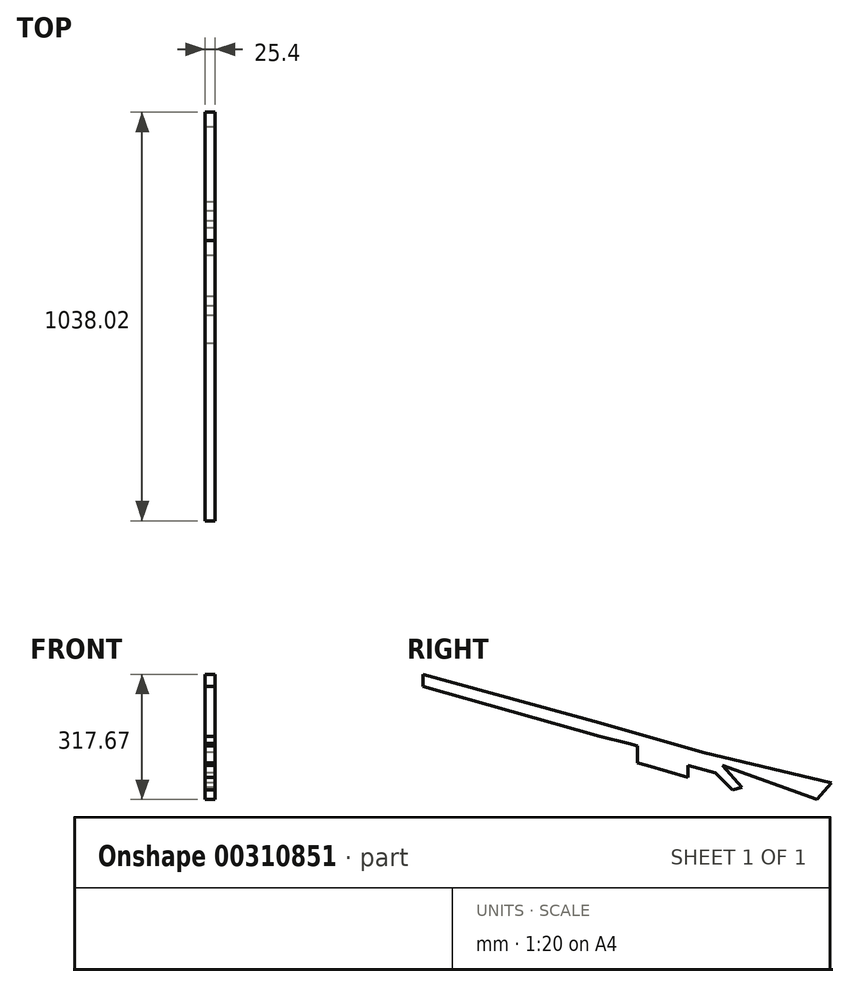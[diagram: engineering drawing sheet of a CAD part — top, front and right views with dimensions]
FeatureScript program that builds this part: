
annotation { "Feature Type Name" : "Feature", "Feature Type Description" : "" }
export const myFeature = defineFeature(function(context is Context, id is Id, definition is map)
    precondition{}
    {
        {
            var Q0;
            Q0=qCreatedBy(makeId("Right.planeOp"),FACE);
            var sketch = newSketch(context, id + "F0", { "sketchPlane" : qUnion([Q0])});
            skLineSegment(sketch, "E0", {"start": v(0, 0) * mm, "end": v(191.87, -55.13) * mm});
            skLineSegment(sketch, "E1", {"start": v(191.87, -55.13) * mm, "end": v(240.84, -111.58) * mm});
            skLineSegment(sketch, "E2", {"start": v(240.84, -111.58) * mm, "end": v(217.53, -117.95) * mm});
            skLineSegment(sketch, "E3", {"start": v(217.53, -117.95) * mm, "end": v(174.26, -75.25) * mm});
            skLineSegment(sketch, "E4", {"start": v(174.26, -75.25) * mm, "end": v(104.37, -55.13) * mm});
            skLineSegment(sketch, "E5", {"start": v(104.37, -55.13) * mm, "end": v(104.37, -86.25) * mm});
            skLineSegment(sketch, "E6", {"start": v(104.37, -86.25) * mm, "end": v(0, -55.13) * mm});
            skLineSegment(sketch, "E7", {"start": v(0, -55.13) * mm, "end": v(0, 0) * mm});
            skLineSegment(sketch, "E8", {"start": v(0, 0) * mm, "end": v(-47.42, 14.1) * mm});
            skLineSegment(sketch, "E9", {"start": v(-47.42, 14.1) * mm, "end": v(-47.42, 0) * mm});
            skLineSegment(sketch, "E10", {"start": v(-47.42, 0) * mm, "end": v(0, -12.5) * mm});
            skLineSegment(sketch, "E11", {"start": v(0, -12.5) * mm, "end": v(0, -55.13) * mm});
            skLineSegment(sketch, "E12", {"start": v(0, -55.13) * mm, "end": v(-23.7, -49.55) * mm});
            skPoint(sketch, "E12.endSnap0", {"position": v(-23.7, -6.25) * mm});
            skLineSegment(sketch, "E13", {"start": v(-23.7, -49.55) * mm, "end": v(-23.7, -6.25) * mm});
            skLineSegment(sketch, "E14", {"start": v(191.87, -55.13) * mm, "end": v(142.53, -22.53) * mm});
            skLineSegment(sketch, "E15", {"start": v(142.53, -22.53) * mm, "end": v(-51.75, 32.66) * mm});
            skLineSegment(sketch, "E16", {"start": v(-51.75, 32.66) * mm, "end": v(-47.42, 14.1) * mm});
            skLineSegment(sketch, "E17", {"start": v(-51.75, 32.66) * mm, "end": v(-119.48, 51.9) * mm});
            skLineSegment(sketch, "E18", {"start": v(-119.48, 51.9) * mm, "end": v(-119.48, 17.83) * mm});
            skLineSegment(sketch, "E19", {"start": v(-119.48, 17.83) * mm, "end": v(-47.42, 0) * mm});
            skLineSegment(sketch, "E20", {"start": v(-119.48, 51.9) * mm, "end": v(-569.33, 175.84) * mm});
            skLineSegment(sketch, "E21", {"start": v(-569.33, 175.84) * mm, "end": v(-569.33, 145.17) * mm});
            skLineSegment(sketch, "E22", {"start": v(-569.33, 145.17) * mm, "end": v(-119.48, 17.83) * mm});
            skLineSegment(sketch, "E23", {"start": v(191.87, -55.13) * mm, "end": v(431.18, -141.83) * mm});
            skLineSegment(sketch, "E24", {"start": v(431.18, -141.83) * mm, "end": v(142.53, -22.53) * mm});
            skLineSegment(sketch, "E25", {"start": v(142.53, -22.53) * mm, "end": v(468.69, -99.6) * mm});
            skLineSegment(sketch, "E26", {"start": v(468.69, -99.6) * mm, "end": v(431.18, -141.83) * mm});
            skSolve(sketch);
        }
        {
            var Q0;
            Q0 = qSketchRegion(id + "F0", true);
            extrude(context, id + "F1", {"entities" : qUnion([Q0]), "depth" : 25.4 * mm});
        }
    });
